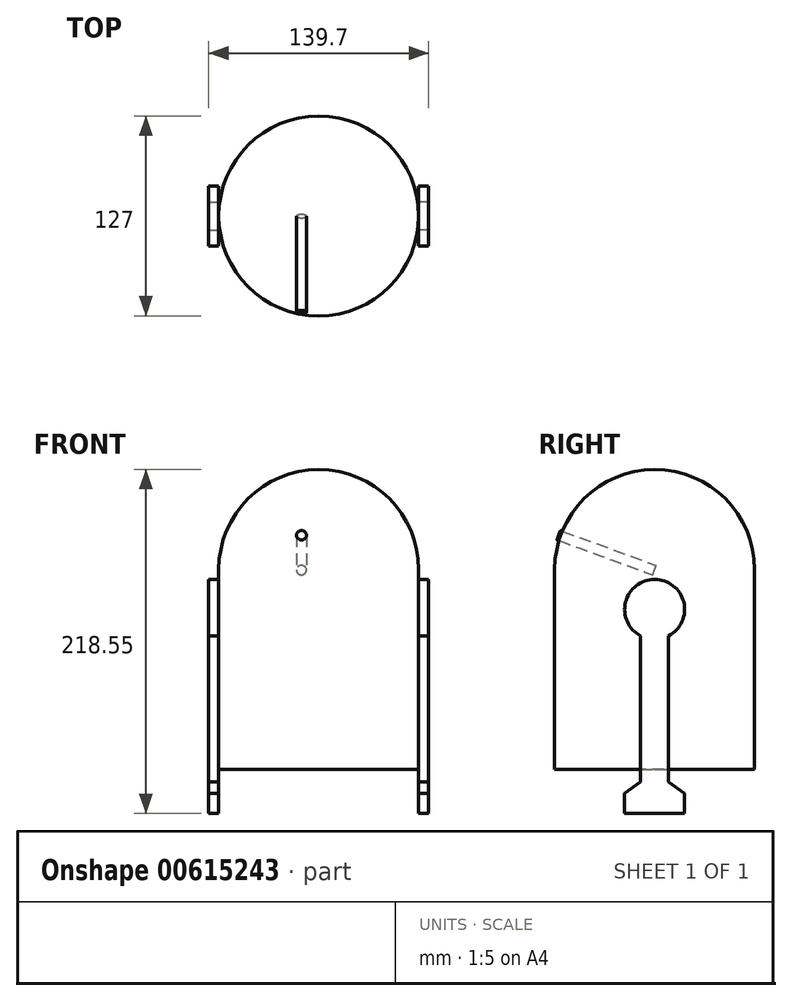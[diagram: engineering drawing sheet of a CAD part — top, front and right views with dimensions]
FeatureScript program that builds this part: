
annotation { "Feature Type Name" : "Feature", "Feature Type Description" : "" }
export const myFeature = defineFeature(function(context is Context, id is Id, definition is map)
    precondition{}
    {
        {
            var Q0;
            Q0=qCreatedBy(makeId("Top.planeOp"),FACE);
            var sketch = newSketch(context, id + "F0", { "sketchPlane" : qUnion([Q0])});
            skCircle(sketch, "E0", {"center": v(0, 0) * mm, "radius": 63.5 * mm});
            skSolve(sketch);
        }
        {
            var Q0;
            Q0=makeQuery(id+"F0.imprint","IMPRINT",FACE,{"disambiguationData":[TD([[makeQuery(id+"F0.imprint","IMPRINT",EDGE,{"derivedFrom":sQuery(id+"F0.wireOp",EDGE,"E0")}),1.0]])]});
            var Q1;
            Q1=sQuery(id+"F0.wireOp",EDGE,"E0");
            extrude(context, id + "F1", {"entities" : qUnion([Q0]), "surfaceEntities" : qUnion([Q1]), "depth" : 127 * mm, "offsetDistance" : 25.4 * mm});
        }
        {
            var Q0;
            Q0=makeQuery(id+"F1.opExtrude","CAP_FACE",FACE,{"disambiguationData":[OSD([sQuery(id+"F0.wireOp",EDGE,"E0")])],"isStart":false});
            var sketch = newSketch(context, id + "F2", { "sketchPlane" : qUnion([Q0])});
            skCircle(sketch, "E1", {"center": v(0, 0) * mm, "radius": 63.5 * mm});
            skLineSegment(sketch, "E2", {"start": v(0, 63.5) * mm, "end": v(0, -63.5) * mm});
            skSolve(sketch);
        }
        {
            var Q0;
            {var subQ0=sQuery(id+"F2.wireOp",EDGE,"E2");Q0=makeQuery(id+"F2.imprint","IMPRINT",FACE,{"disambiguationData":[TD([[makeQuery(id+"F2.imprint","IMPRINT",EDGE,{"derivedFrom":subQ0}),-1.0]])]});}
            var Q1;
            Q1=sQuery(id+"F2.wireOp",EDGE,"E2");
            revolve(context, id + "F3", {"operationType" : NewBodyOperationType.ADD, "entities" : qUnion([Q0]), "axis" : qUnion([Q1]), "revolveType" : RevolveType.FULL});
        }
        {
            var Q0;
            Q0=qCreatedBy(makeId("Right.planeOp"),FACE);
            cPlane(context, id + "F4", {"entities" : qUnion([Q0]), "cplaneType" : CPlaneType.OFFSET, "offset" : 63.5 * mm, "width" : 152.4 * mm, "height" : 152.4 * mm});
        }
        {
            var Q0;
            Q0=qCreatedBy(id+"F4.planeOp",FACE);
            var sketch = newSketch(context, id + "F5", { "sketchPlane" : qUnion([Q0])});
            skCircle(sketch, "E3", {"center": v(0, 101.6) * mm, "radius": 19.05 * mm});
            skLineSegment(sketch, "E4.left", {"start": v(-8.9, 84.75) * mm, "end": v(-8.89, -8.04) * mm});
            skLineSegment(sketch, "E4.right", {"start": v(8.89, 84.75) * mm, "end": v(8.9, -8.04) * mm});
            skLineSegment(sketch, "E5", {"start": v(-8.89, -8.04) * mm, "end": v(-19.05, -15.35) * mm});
            skLineSegment(sketch, "E6", {"start": v(-19.05, -15.35) * mm, "end": v(-19.05, -28.05) * mm});
            skLineSegment(sketch, "E7", {"start": v(-19.05, -28.05) * mm, "end": v(19.05, -28.05) * mm});
            skLineSegment(sketch, "E8", {"start": v(19.05, -28.05) * mm, "end": v(19.05, -15.35) * mm});
            skLineSegment(sketch, "E9", {"start": v(19.05, -15.35) * mm, "end": v(8.9, -8.04) * mm});
            skSolve(sketch);
        }
        {
            var Q0;
            {var subQ0=sQuery(id+"F5.wireOp",EDGE,"E3");var subQ1=makeQuery(id+"F5.imprint","INTERSECT",VERTEX,{"derivedFrom":[subQ0,sQuery(id+"F5.wireOp",EDGE,"E4.left")]});Q0=makeQuery(id+"F5.imprint","IMPRINT",FACE,{"disambiguationData":[TD([[makeQuery(id+"F5.imprint","IMPRINT",EDGE,{"disambiguationData":[TD([[subQ1,-1.0]])],"derivedFrom":subQ0}),1.0]])]});}
            var Q1;
            {var subQ1=sQuery(id+"F5.wireOp",EDGE,"E4.left");Q1=makeQuery(id+"F5.imprint","IMPRINT",FACE,{"disambiguationData":[TD([[makeQuery(id+"F5.imprint","IMPRINT",EDGE,{"derivedFrom":subQ1}),1.0]])]});}
            extrude(context, id + "F6", {"entities" : qUnion([Q0, Q1]), "operationType" : NewBodyOperationType.ADD, "depth" : 6.35 * mm, "offsetDistance" : 25.4 * mm});
        }
        {
            var Q0;
            Q0=makeQuery(id+"F6.opExtrude","SWEPT_BODY",BODY,{"disambiguationData":[OSD([sQuery(id+"F5.wireOp",EDGE,"E3"),sQuery(id+"F5.wireOp",EDGE,"E4.left"),sQuery(id+"F5.wireOp",EDGE,"E4.right"),sQuery(id+"F5.wireOp",EDGE,"E5"),sQuery(id+"F5.wireOp",EDGE,"E6"),sQuery(id+"F5.wireOp",EDGE,"E7"),sQuery(id+"F5.wireOp",EDGE,"E8"),sQuery(id+"F5.wireOp",EDGE,"E9")])]});
            var Q1;
            Q1=qCreatedBy(makeId("Right.planeOp"),FACE);
            mirror(context, id + "F7", {"entities" : qUnion([Q0]), "mirrorPlane" : qUnion([Q1])});
        }
        {
            var Q0;
            {var subQ0=sQuery(id+"F2.wireOp",EDGE,"E2");Q0=makeQuery(id+"F2.imprint","IMPRINT",FACE,{"disambiguationData":[TD([[makeQuery(id+"F2.imprint","IMPRINT",EDGE,{"derivedFrom":subQ0}),1.0]])]});}
            var sketch = newSketch(context, id + "F8", { "sketchPlane" : qUnion([Q0])});
            skLineSegment(sketch, "E10", {"start": v(0, 0) * mm, "end": v(52.1, 0) * mm});
            skSolve(sketch);
        }
        {
            var Q0;
            Q0=sQuery(id+"F8.wireOp",EDGE,"E10");
            cPlane(context, id + "F9", {"entities" : qUnion([Q0]), "cplaneType" : CPlaneType.LINE_ANGLE, "offset" : 25.4 * mm, "angle" : 160 * degree, "width" : 152.4 * mm, "height" : 152.4 * mm});
        }
        {
            var Q0;
            Q0=qCreatedBy(id+"F9.planeOp",FACE);
            var sketch = newSketch(context, id + "F10", { "sketchPlane" : qUnion([Q0])});
            skCircle(sketch, "E11", {"center": v(-10.99, 118.85) * mm, "radius": 3.18 * mm});
            skSolve(sketch);
        }
        {
            var Q0;
            Q0=makeQuery(id+"F10.imprint","IMPRINT",FACE,{"disambiguationData":[TD([[makeQuery(id+"F10.imprint","IMPRINT",EDGE,{"derivedFrom":sQuery(id+"F10.wireOp",EDGE,"E11")}),1.0]])]});
            extrude(context, id + "F11", {"entities" : qUnion([Q0]), "depth" : 64.77 * mm, "offsetDistance" : 25.4 * mm});
        }
    });
